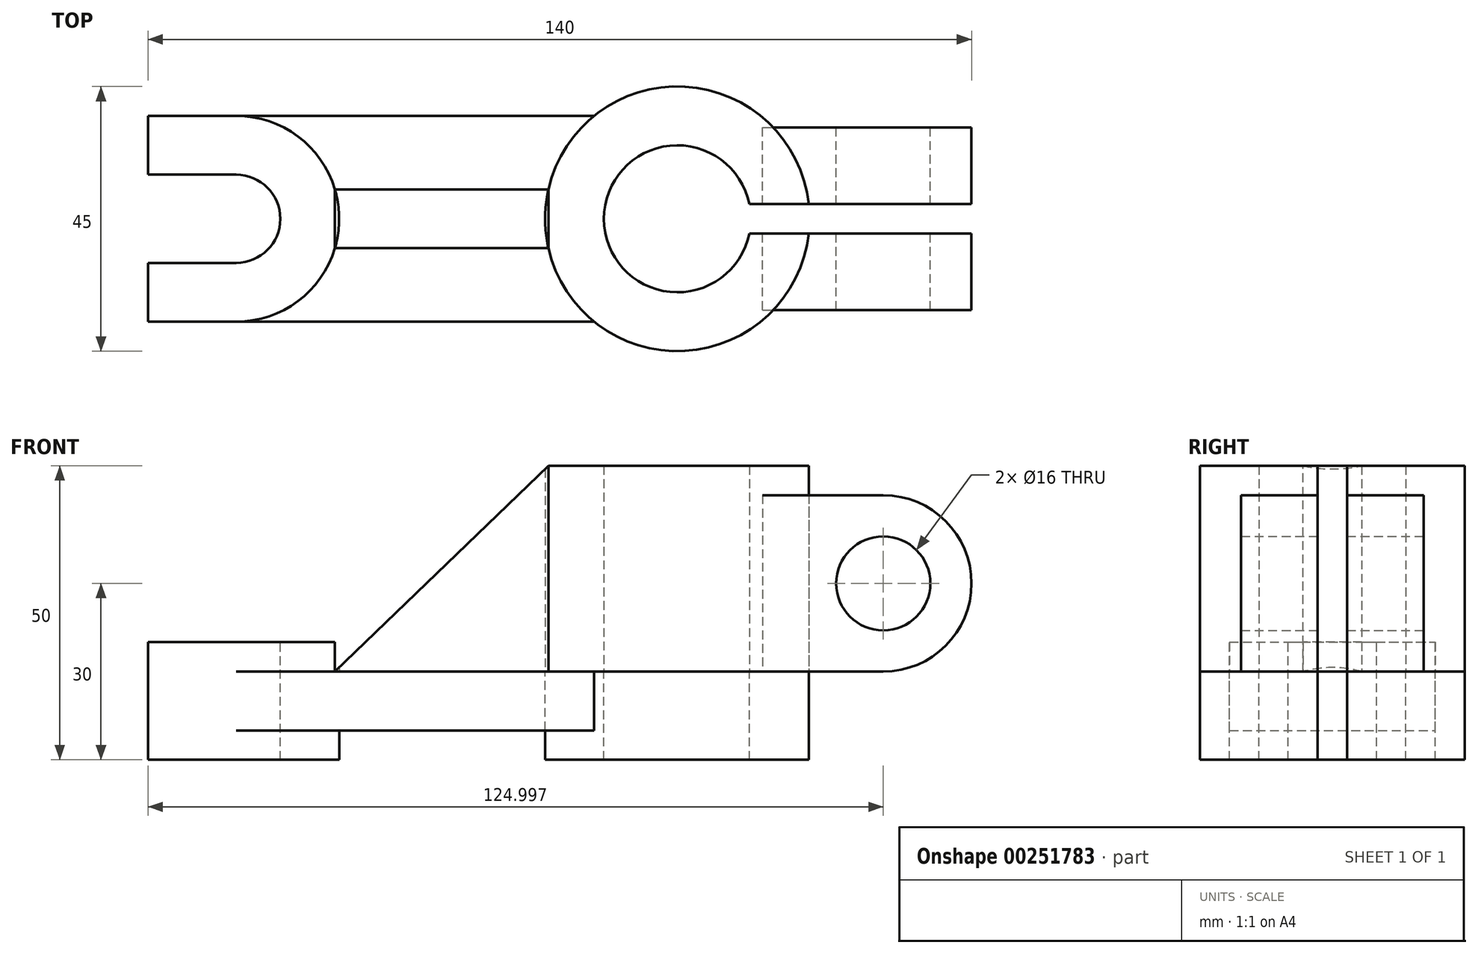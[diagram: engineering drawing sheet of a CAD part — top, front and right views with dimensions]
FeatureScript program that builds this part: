
annotation { "Feature Type Name" : "Feature", "Feature Type Description" : "" }
export const myFeature = defineFeature(function(context is Context, id is Id, definition is map)
    precondition{}
    {
        {
            var Q0;
            Q0=qCreatedBy(makeId("Front.planeOp"),FACE);
            var sketch = newSketch(context, id + "F0", { "sketchPlane" : qUnion([Q0])});
            skLineSegment(sketch, "E0.bottom", {"start": v(42.73, -5) * mm, "end": v(-47.27, -5) * mm});
            skLineSegment(sketch, "E0.top", {"start": v(42.73, 5) * mm, "end": v(-47.27, 5) * mm});
            skLineSegment(sketch, "E0.left", {"start": v(42.73, -5) * mm, "end": v(42.73, 5) * mm});
            skLineSegment(sketch, "E0.right", {"start": v(-47.27, -5) * mm, "end": v(-47.27, 5) * mm});
            skPoint(sketch, "E0.middle", {"position": v(-2.27, 0) * mm});
            skSolve(sketch);
        }
        {
            var Q0;
            Q0 = qSketchRegion(id + "F0", true);
            extrude(context, id + "F1", {"entities" : qUnion([Q0]), "endBound" : BoundingType.SYMMETRIC, "depth" : 35 * mm});
        }
        {
            var Q0;
            Q0=makeQuery(id+"F1.opExtrude","SWEPT_FACE",FACE,{"disambiguationData":[OSD([sQuery(id+"F0.wireOp",EDGE,"E0.top")])]});
            var sketch = newSketch(context, id + "F2", { "sketchPlane" : qUnion([Q0])});
            skLineSegment(sketch, "E1.left", {"start": v(-47.27, 7.5) * mm, "end": v(-47.27, -9.01) * mm});
            skArc(sketch, "E2", {"start": v(-32.27, -7.5) * mm, "mid": v(-24.77, 0) * mm, "end": v(-32.27, 7.5) * mm});
            skLineSegment(sketch, "E3", {"start": v(-32.27, -7.5) * mm, "end": v(-48.08, -7.5) * mm});
            skLineSegment(sketch, "E4", {"start": v(-32.27, 7.5) * mm, "end": v(-47.27, 7.5) * mm});
            skPoint(sketch, "E1.bottom.end.orphan", {"position": v(-32.27, 17.5) * mm});
            skPoint(sketch, "E5.orphan", {"position": v(-47.27, 17.5) * mm});
            skPoint(sketch, "E1.top.end.orphan", {"position": v(-32.27, -17.5) * mm});
            skSolve(sketch);
        }
        {
            var Q0;
            Q0 = qSketchRegion(id + "F2", true);
            extrude(context, id + "F3", {"entities" : qUnion([Q0]), "operationType" : NewBodyOperationType.REMOVE, "endBound" : BoundingType.THROUGH_ALL, "oppositeDirection" : true, "depth" : 25 * mm});
        }
        {
            var Q0;
            Q0=makeQuery(id+"F1.opExtrude","SWEPT_FACE",FACE,{"disambiguationData":[OSD([sQuery(id+"F0.wireOp",EDGE,"E0.top")])]});
            var sketch = newSketch(context, id + "F4", { "sketchPlane" : qUnion([Q0])});
            skArc(sketch, "E6", {"start": v(-32.27, -17.5) * mm, "mid": v(-14.77, 0) * mm, "end": v(-32.27, 17.5) * mm});
            skLineSegment(sketch, "E7.0", {"start": v(-32.27, 17.5) * mm, "end": v(-47.27, 17.5) * mm});
            skLineSegment(sketch, "E8.0", {"start": v(-32.27, -17.5) * mm, "end": v(-47.27, -17.5) * mm});
            skArc(sketch, "E9.0", {"start": v(-32.27, -7.5) * mm, "mid": v(-24.77, 0) * mm, "end": v(-32.27, 7.5) * mm});
            skLineSegment(sketch, "E10.0", {"start": v(-32.27, 7.5) * mm, "end": v(-47.27, 7.5) * mm});
            skLineSegment(sketch, "E11.0", {"start": v(-47.27, 7.5) * mm, "end": v(-47.27, 17.5) * mm});
            skLineSegment(sketch, "E12.0", {"start": v(-47.27, -17.5) * mm, "end": v(-47.27, -7.5) * mm});
            skLineSegment(sketch, "E13.0", {"start": v(-32.27, -7.5) * mm, "end": v(-47.27, -7.5) * mm});
            skPoint(sketch, "E14.orphan", {"position": v(42.73, 17.5) * mm});
            skPoint(sketch, "E15.orphan", {"position": v(42.73, -17.5) * mm});
            skSolve(sketch);
        }
        {
            var Q0;
            Q0 = qSketchRegion(id + "F4", true);
            extrude(context, id + "F5", {"entities" : qUnion([Q0]), "operationType" : NewBodyOperationType.ADD, "depth" : 5 * mm});
        }
        {
            var Q0;
            Q0=makeQuery(id+"F1.opExtrude","SWEPT_FACE",FACE,{"disambiguationData":[OSD([sQuery(id+"F0.wireOp",EDGE,"E0.bottom")])]});
            var sketch = newSketch(context, id + "F6", { "sketchPlane" : qUnion([Q0])});
            skArc(sketch, "E16.0", {"start": v(-32.27, 17.5) * mm, "mid": v(-14.77, 0) * mm, "end": v(-32.27, -17.5) * mm});
            skLineSegment(sketch, "E17.0", {"start": v(-32.27, 17.5) * mm, "end": v(-47.27, 17.5) * mm});
            skLineSegment(sketch, "E18.0.0", {"start": v(-32.27, -7.5) * mm, "end": v(-47.27, -7.5) * mm});
            skLineSegment(sketch, "E18.0.1", {"start": v(-47.27, -7.5) * mm, "end": v(-47.27, -17.5) * mm});
            skLineSegment(sketch, "E18.0.2", {"start": v(-47.27, -17.5) * mm, "end": v(-32.27, -17.5) * mm});
            skLineSegment(sketch, "E18.0.5", {"start": v(-47.27, 17.5) * mm, "end": v(-47.27, 7.5) * mm});
            skLineSegment(sketch, "E18.0.6", {"start": v(-47.27, 7.5) * mm, "end": v(-32.27, 7.5) * mm});
            skArc(sketch, "E18.0.7", {"start": v(-32.27, 7.5) * mm, "mid": v(-24.77, 0) * mm, "end": v(-32.27, -7.5) * mm});
            skPoint(sketch, "E18.0.3.end.orphan", {"position": v(42.73, 17.5) * mm});
            skPoint(sketch, "E18.0.3.start.orphan", {"position": v(42.73, -17.5) * mm});
            skSolve(sketch);
        }
        {
            var Q0;
            Q0 = qSketchRegion(id + "F6", true);
            extrude(context, id + "F7", {"entities" : qUnion([Q0]), "operationType" : NewBodyOperationType.ADD, "depth" : 5 * mm});
        }
        {
            var Q0;
            Q0=makeQuery(id+"F1.opExtrude","SWEPT_FACE",FACE,{"disambiguationData":[OSD([sQuery(id+"F0.wireOp",EDGE,"E0.top")])]});
            var sketch = newSketch(context, id + "F8", { "sketchPlane" : qUnion([Q0])});
            skCircle(sketch, "E19", {"center": v(42.73, 0) * mm, "radius": 22.5 * mm});
            skCircle(sketch, "E20", {"center": v(42.73, 0) * mm, "radius": 12.5 * mm});
            skSolve(sketch);
        }
        {
            var Q0;
            Q0 = qSketchRegion(id + "F8", true);
            extrude(context, id + "F9", {"entities" : qUnion([Q0]), "operationType" : NewBodyOperationType.ADD, "depth" : 35 * mm});
        }
        {
            var Q0;
            Q0 = qSketchRegion(id + "F8", true);
            extrude(context, id + "F10", {"entities" : qUnion([Q0]), "operationType" : NewBodyOperationType.REMOVE, "endBound" : BoundingType.THROUGH_ALL, "oppositeDirection" : true, "depth" : 25 * mm});
        }
        {
            var Q0;
            Q0=makeQuery(id+"F10.boolean.opBoolean","SPLIT",FACE,{"disambiguationData":[TD([makeQuery(id+"F1.opExtrude","SWEPT_FACE",FACE,{"disambiguationData":[OSD([sQuery(id+"F0.wireOp",EDGE,"E0.left")])]})])],"derivedFrom":makeQuery(id+"F1.opExtrude","SWEPT_FACE",FACE,{"disambiguationData":[OSD([sQuery(id+"F0.wireOp",EDGE,"E0.bottom")])]})});
            extrude(context, id + "F11", {"entities" : qUnion([Q0]), "operationType" : NewBodyOperationType.REMOVE, "endBound" : BoundingType.THROUGH_ALL, "oppositeDirection" : true, "depth" : 25 * mm});
        }
        {
            var Q0;
            {var subQ0=sQuery(id+"F8.wireOp",EDGE,"E20");var subQ1=sQuery(id+"F8.wireOp",EDGE,"E19");Q0=makeQuery(id+"F10.boolean.opBoolean","MERGE",FACE,{"derivedFrom":[makeQuery(id+"F9.opExtrude","CAP_FACE",FACE,{"disambiguationData":[OSD([subQ1,subQ0])],"isStart":true}),makeQuery(id+"F10.opExtrude","CAP_FACE",FACE,{"disambiguationData":[OSD([subQ1,subQ0])],"isStart":true})]});}
            extrude(context, id + "F12", {"entities" : qUnion([Q0]), "depth" : 15 * mm});
        }
        {
            var Q0;
            {var subQ3=sQuery(id+"F0.wireOp",EDGE,"E0.top");Q0=makeQuery(id+"F9.boolean.opBoolean","SPLIT",FACE,{"disambiguationData":[TD([makeQuery(id+"F5.opExtrude","SWEPT_FACE",FACE,{"disambiguationData":[OSD([sQuery(id+"F4.wireOp",EDGE,"E6")])]})])],"derivedFrom":makeQuery(id+"F1.opExtrude","SWEPT_FACE",FACE,{"disambiguationData":[OSD([subQ3])]})});}
            var sketch = newSketch(context, id + "F13", { "sketchPlane" : qUnion([Q0])});
            skLineSegment(sketch, "E21.bottom", {"start": v(20.79, -5) * mm, "end": v(-15.5, -5) * mm});
            skLineSegment(sketch, "E21.top", {"start": v(20.79, 5) * mm, "end": v(-15.5, 5) * mm});
            skPoint(sketch, "E21.middle", {"position": v(0, 0) * mm});
            skArc(sketch, "E22.0", {"start": v(20.79, 5) * mm, "mid": v(20.23, 0) * mm, "end": v(20.79, -5) * mm});
            skArc(sketch, "E23.0", {"start": v(-15.5, -5) * mm, "mid": v(-14.77, 0) * mm, "end": v(-15.5, 5) * mm});
            skPoint(sketch, "E24.orphan", {"position": v(24.34, 5) * mm});
            skPoint(sketch, "E25.orphan", {"position": v(24.34, -5) * mm});
            skPoint(sketch, "E21.right.end.orphan", {"position": v(-24.34, 5) * mm});
            skPoint(sketch, "E21.right.start.orphan", {"position": v(-24.34, -5) * mm});
            skPoint(sketch, "E26.orphan", {"position": v(-32.27, 17.5) * mm});
            skPoint(sketch, "E27.orphan", {"position": v(-32.27, -17.5) * mm});
            skSolve(sketch);
        }
        {
            var Q0;
            Q0 = qSketchRegion(id + "F13", true);
            extrude(context, id + "F14", {"entities" : qUnion([Q0]), "depth" : 35 * mm});
        }
        {
            var Q0;
            Q0=makeQuery(id+"F14.opExtrude","SWEPT_FACE",FACE,{"disambiguationData":[OSD([sQuery(id+"F13.wireOp",EDGE,"E21.bottom")])]});
            var sketch = newSketch(context, id + "F15", { "sketchPlane" : qUnion([Q0])});
            skLineSegment(sketch, "E28", {"start": v(-15.5, 5) * mm, "end": v(20.79, 40) * mm});
            skLineSegment(sketch, "E29.0", {"start": v(20.79, 40) * mm, "end": v(-15.5, 40) * mm});
            skLineSegment(sketch, "E30.0", {"start": v(-15.5, 40) * mm, "end": v(-15.5, 5) * mm});
            skSolve(sketch);
        }
        {
            var Q0;
            Q0 = qSketchRegion(id + "F15", true);
            extrude(context, id + "F16", {"entities" : qUnion([Q0]), "operationType" : NewBodyOperationType.REMOVE, "endBound" : BoundingType.THROUGH_ALL, "oppositeDirection" : true, "depth" : 25 * mm});
        }
        {
            var Q0;
            Q0=qCreatedBy(makeId("Front.planeOp"),FACE);
            var sketch = newSketch(context, id + "F17", { "sketchPlane" : qUnion([Q0])});
            skLineSegment(sketch, "E31.bottom", {"start": v(57.21, 35) * mm, "end": v(77.73, 35) * mm});
            skLineSegment(sketch, "E31.top", {"start": v(57.21, 5) * mm, "end": v(77.73, 5) * mm});
            skLineSegment(sketch, "E31.left", {"start": v(57.21, 35) * mm, "end": v(57.21, 5) * mm});
            skLineSegment(sketch, "E31.right", {"start": v(77.73, 35) * mm, "end": v(77.73, 5) * mm});
            skLineSegment(sketch, "E32", {"start": v(65.23, 28.3) * mm, "end": v(65.23, 11.7) * mm});
            skArc(sketch, "E33", {"start": v(65.23, 11.7) * mm, "mid": v(92.73, 20) * mm, "end": v(65.23, 28.3) * mm});
            skCircle(sketch, "E34", {"center": v(77.73, 20) * mm, "radius": 8 * mm});
            skLineSegment(sketch, "E35", {"start": v(42.73, 40) * mm, "end": v(42.73, -24.52) * mm, "construction": true});
            skLineSegment(sketch, "E36", {"start": v(77.73, 20) * mm, "end": v(13.99, 20) * mm, "construction": true});
            skPoint(sketch, "E36.endSnap0", {"position": v(57.21, 20) * mm});
            skPoint(sketch, "E37.orphan", {"position": v(30.23, 5) * mm});
            skPoint(sketch, "E38.end.orphan", {"position": v(30.23, 40) * mm});
            skPoint(sketch, "E39.orphan", {"position": v(20.23, 40) * mm});
            skPoint(sketch, "E40.0.end.orphan", {"position": v(65.23, 40) * mm});
            skPoint(sketch, "E41.orphan", {"position": v(55.23, 40) * mm});
            skPoint(sketch, "E42.end.orphan", {"position": v(55.23, 5) * mm});
            skSolve(sketch);
        }
        {
            var Q0;
            Q0 = qSketchRegion(id + "F17", true);
            extrude(context, id + "F18", {"entities" : qUnion([Q0]), "endBound" : BoundingType.SYMMETRIC, "depth" : 31 * mm});
        }
        {
            var Q0;
            Q0=makeQuery(id+"F9.opExtrude","CAP_FACE",FACE,{"disambiguationData":[OSD([sQuery(id+"F8.wireOp",EDGE,"E19"),sQuery(id+"F8.wireOp",EDGE,"E20")])],"isStart":false});
            var sketch = newSketch(context, id + "F19", { "sketchPlane" : qUnion([Q0])});
            skLineSegment(sketch, "E43.bottom", {"start": v(42.73, 2.5) * mm, "end": v(97.73, 2.5) * mm});
            skLineSegment(sketch, "E43.top", {"start": v(42.73, -2.5) * mm, "end": v(97.73, -2.5) * mm});
            skLineSegment(sketch, "E43.left", {"start": v(42.73, 2.5) * mm, "end": v(42.73, -2.5) * mm});
            skLineSegment(sketch, "E43.right", {"start": v(97.73, 2.5) * mm, "end": v(97.73, -2.5) * mm});
            skSolve(sketch);
        }
        {
            var Q0;
            Q0 = qSketchRegion(id + "F19", true);
            extrude(context, id + "F20", {"entities" : qUnion([Q0]), "operationType" : NewBodyOperationType.REMOVE, "endBound" : BoundingType.THROUGH_ALL, "oppositeDirection" : true, "depth" : 25 * mm});
        }
        {
            var Q0;
            Q0=makeQuery(id+"F18.opExtrude","SWEPT_FACE",FACE,{"disambiguationData":[OSD([sQuery(id+"F17.wireOp",EDGE,"E31.bottom")])]});
            var sketch = newSketch(context, id + "F21", { "sketchPlane" : qUnion([Q0])});
            skLineSegment(sketch, "E44.bottom", {"start": v(42.73, -2.5) * mm, "end": v(105.73, -2.5) * mm});
            skLineSegment(sketch, "E44.top", {"start": v(42.73, 2.5) * mm, "end": v(105.73, 2.5) * mm});
            skLineSegment(sketch, "E44.left", {"start": v(42.73, -2.5) * mm, "end": v(42.73, 2.5) * mm});
            skLineSegment(sketch, "E44.right", {"start": v(105.73, -2.5) * mm, "end": v(105.73, 2.5) * mm});
            skSolve(sketch);
        }
        {
            var Q0;
            Q0 = qSketchRegion(id + "F21", true);
            extrude(context, id + "F22", {"entities" : qUnion([Q0]), "operationType" : NewBodyOperationType.REMOVE, "endBound" : BoundingType.THROUGH_ALL, "oppositeDirection" : true, "depth" : 25 * mm});
        }
    });
